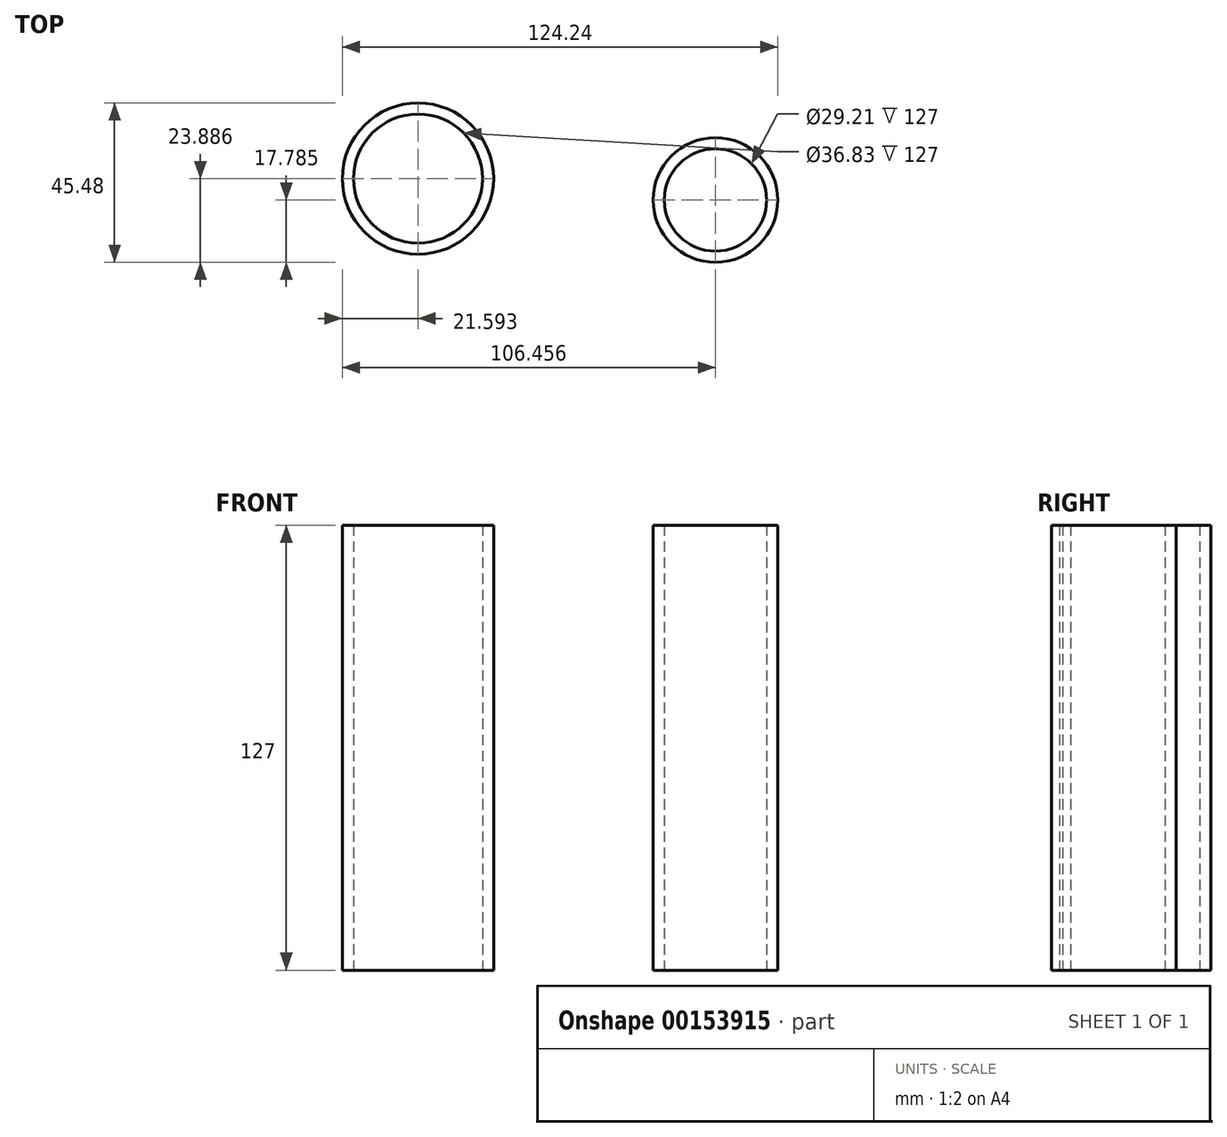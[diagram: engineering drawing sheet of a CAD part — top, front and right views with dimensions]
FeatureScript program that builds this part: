
annotation { "Feature Type Name" : "Feature", "Feature Type Description" : "" }
export const myFeature = defineFeature(function(context is Context, id is Id, definition is map)
    precondition{}
    {
        {
            var Q0;
            Q0=qCreatedBy(makeId("Top.planeOp"),FACE);
            var sketch = newSketch(context, id + "F0", { "sketchPlane" : qUnion([Q0])});
            skCircle(sketch, "E0", {"center": v(-37.72, 29.54) * mm, "radius": 21.59 * mm});
            skCircle(sketch, "E1", {"center": v(-37.72, 29.54) * mm, "radius": 18.41 * mm});
            skSolve(sketch);
        }
        {
            var Q0;
            Q0 = qSketchRegion(id + "F0", true);
            extrude(context, id + "F1", {"entities" : qUnion([Q0]), "depth" : 127 * mm});
        }
        {
            var Q0;
            Q0=qCreatedBy(makeId("Top.planeOp"),FACE);
            var sketch = newSketch(context, id + "F2", { "sketchPlane" : qUnion([Q0])});
            skCircle(sketch, "E2", {"center": v(47.15, 23.43) * mm, "radius": 17.78 * mm});
            skCircle(sketch, "E3", {"center": v(47.15, 23.43) * mm, "radius": 14.6 * mm});
            skSolve(sketch);
        }
        {
            var Q0;
            Q0 = qSketchRegion(id + "F2", true);
            extrude(context, id + "F3", {"entities" : qUnion([Q0]), "depth" : 127 * mm});
        }
    });
